# Revit family: 01871-G
name_source: partatom
category: Instalační zařizovací předměty
revit_build: Autodesk Revit 2016 (Build: 20161004_0715(x64)
units: mm (PartAtom-declared; Revit-internal decimal feet)

## family parameters
Bod výpočtu místnosti = Ne
Kóta kulaté spojky = Použít průměr
Nadpis OmniClass = Sanitary Equipment
Ořezat dutým tvarem při načtení = Ne
Sdílené = Ne
Typ součásti = Normální
Vždy vertikální = Ano
Založené na pracovní rovině = Ne
Číslo OmniClass = 23.45.05.00

## types (1)
- 01871-G
    Article number = 01871.G
    DEPTH = 177 mm  [stored 0.580709 ft]
    HEIGHT = 277 mm  [stored 0.908793 ft]
    IP code = IP22
    MATERIAL = <Podle kategorie>
    Noise level = 65
    Power input = 0 W
    Power supply = 0 V
    Připojení CW = Ne
    Připojení HW = Ne
    Připojení odpadu = Ne
    Připojení ventilace = Ne
    Surface finish = Gray
    Utility frequency = 0
    Výrobce = Nofer
    WEIGHT = 3.00 kg
    WIDTH = 164 mm  [stored 0.538058 ft]

note: [stored X ft] marks values corroborated as IEEE doubles in the binary element streams (Revit-internal decimal feet)
